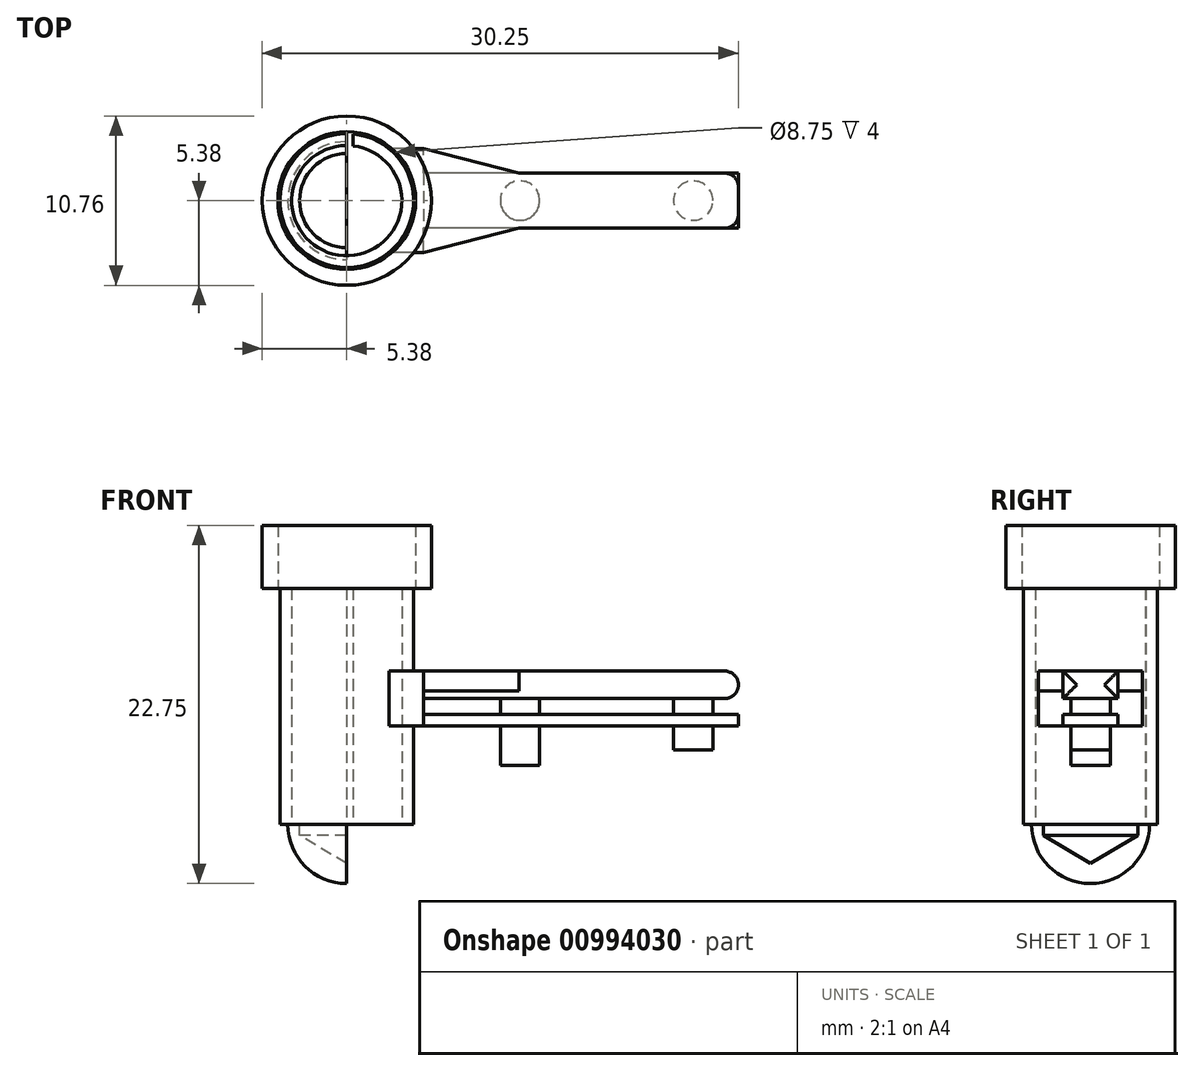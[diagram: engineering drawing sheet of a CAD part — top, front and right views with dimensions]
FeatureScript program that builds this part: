
annotation { "Feature Type Name" : "Feature", "Feature Type Description" : "" }
export const myFeature = defineFeature(function(context is Context, id is Id, definition is map)
    precondition{}
    {
        {
            var Q0;
            Q0=qCreatedBy(makeId("Top.planeOp"),FACE);
            var sketch = newSketch(context, id + "F0", { "sketchPlane" : qUnion([Q0])});
            skCircle(sketch, "E0", {"center": v(0, 0) * mm, "radius": 3.5 * mm});
            skCircle(sketch, "E1", {"center": v(0, 0) * mm, "radius": 4.25 * mm});
            skLineSegment(sketch, "E2", {"start": v(0, -4.25) * mm, "end": v(0, 4.25) * mm});
            skLineSegment(sketch, "E3.bottom", {"start": v(0, 4.35) * mm, "end": v(0.4, 4.35) * mm});
            skLineSegment(sketch, "E3.top", {"start": v(0, 3.35) * mm, "end": v(0.4, 3.35) * mm});
            skLineSegment(sketch, "E3.left", {"start": v(0, 4.35) * mm, "end": v(0, 3.35) * mm});
            skLineSegment(sketch, "E3.right", {"start": v(0.4, 4.35) * mm, "end": v(0.4, 3.35) * mm});
            skSolve(sketch);
        }
        {
            var Q0;
            {var subQ0=sQuery(id+"F0.wireOp",EDGE,"E2");var subQ1=sQuery(id+"F0.wireOp",EDGE,"E0");var subQ2=makeQuery(id+"F0.imprint","INTERSECT",VERTEX,{"disambiguationData":[OD(0.0)],"derivedFrom":[subQ1,subQ0]});Q0=makeQuery(id+"F0.imprint","IMPRINT",FACE,{"disambiguationData":[TD([[makeQuery(id+"F0.imprint","IMPRINT",EDGE,{"disambiguationData":[TD([[subQ2,-1.0]])],"derivedFrom":subQ1}),-1.0]])]});}
            var Q1;
            {var subQ0=sQuery(id+"F0.wireOp",EDGE,"E2");var subQ1=sQuery(id+"F0.wireOp",EDGE,"E0");var subQ2=makeQuery(id+"F0.imprint","INTERSECT",VERTEX,{"disambiguationData":[OD(0.0)],"derivedFrom":[subQ1,subQ0]});Q1=makeQuery(id+"F0.imprint","IMPRINT",FACE,{"disambiguationData":[TD([[makeQuery(id+"F0.imprint","IMPRINT",EDGE,{"disambiguationData":[TD([[subQ2,1.0]])],"derivedFrom":subQ1}),-1.0]])]});}
            extrude(context, id + "F1", {"entities" : qUnion([Q0, Q1]), "endBound" : BoundingType.SYMMETRIC, "depth" : 15 * mm, "offsetDistance" : 25 * mm});
        }
        {
            var Q0;
            Q0=qCreatedBy(makeId("Top.planeOp"),FACE);
            cPlane(context, id + "F2", {"entities" : qUnion([Q0]), "cplaneType" : CPlaneType.OFFSET, "offset" : 7.5 * mm, "oppositeDirection" : true, "width" : 150 * mm, "height" : 150 * mm});
        }
        {
            var Q0;
            Q0=qCreatedBy(id+"F2.planeOp",FACE);
            var sketch = newSketch(context, id + "F3", { "sketchPlane" : qUnion([Q0])});
            skPoint(sketch, "E4.end.orphan", {"position": v(0, -3.75) * mm});
            skPoint(sketch, "E4.start.orphan", {"position": v(0, 3.75) * mm});
            skLineSegment(sketch, "E5.left", {"start": v(0, -3.75) * mm, "end": v(0, -3.75) * mm});
            skLineSegment(sketch, "E6.right", {"start": v(0, 3.75) * mm, "end": v(0, 3.75) * mm});
            skArc(sketch, "E7", {"start": v(0, 3.75) * mm, "mid": v(-3.75, 0) * mm, "end": v(0, -3.75) * mm});
            skLineSegment(sketch, "E8", {"start": v(0, 3.75) * mm, "end": v(0, -3.75) * mm});
            skSolve(sketch);
        }
        {
            var Q0;
            Q0=qCreatedBy(makeId("Top.planeOp"),FACE);
            var sketch = newSketch(context, id + "F4", { "sketchPlane" : qUnion([Q0])});
            skLineSegment(sketch, "E9.bottom", {"start": v(4.87, -3.3) * mm, "end": v(0, -3.3) * mm});
            skLineSegment(sketch, "E9.top", {"start": v(4.87, 3.3) * mm, "end": v(0, 3.3) * mm});
            skLineSegment(sketch, "E9.left", {"start": v(4.87, -3.3) * mm, "end": v(4.87, 3.3) * mm});
            skPoint(sketch, "E9.middle", {"position": v(0, 0) * mm});
            skLineSegment(sketch, "E10", {"start": v(0, 3.3) * mm, "end": v(0, -3.3) * mm});
            skSolve(sketch);
        }
        {
            var Q0;
            Q0=qSketchRegion(id+"F4",true);
            extrude(context, id + "F5", {"entities" : qUnion([Q0]), "operationType" : NewBodyOperationType.ADD, "endBound" : BoundingType.SYMMETRIC, "depth" : 2.5 * mm, "offsetDistance" : 25 * mm});
        }
        {
            var Q0;
            Q0=qCreatedBy(makeId("Top.planeOp"),FACE);
            cPlane(context, id + "F6", {"entities" : qUnion([Q0]), "cplaneType" : CPlaneType.OFFSET, "offset" : 2.18 * mm, "oppositeDirection" : true, "width" : 150 * mm, "height" : 150 * mm});
        }
        {
            var Q0;
            Q0=qCreatedBy(id+"F6.planeOp",FACE);
            var sketch = newSketch(context, id + "F7", { "sketchPlane" : qUnion([Q0])});
            skPoint(sketch, "E11", {"position": v(0, 0) * mm});
            skCircle(sketch, "E12", {"center": v(0, 0) * mm, "radius": 15.5 * mm});
            skSolve(sketch);
        }
        {
            var Q0;
            Q0=makeQuery(id+"F5.opExtrude","SWEPT_FACE",FACE,{"disambiguationData":[OSD([sQuery(id+"F4.wireOp",EDGE,"E9.left")])]});
            cPlane(context, id + "F8", {"entities" : qUnion([Q0]), "cplaneType" : CPlaneType.OFFSET, "offset" : 0 * mm, "width" : 150 * mm, "height" : 150 * mm});
        }
        {
            var Q0;
            Q0=qCreatedBy(id+"F8.planeOp",FACE);
            var sketch = newSketch(context, id + "F9", { "sketchPlane" : qUnion([Q0])});
            skLineSegment(sketch, "E13.bottom", {"start": v(1.75, 0.5) * mm, "end": v(-1.75, 0.5) * mm});
            skLineSegment(sketch, "E13.top", {"start": v(1.75, 1.25) * mm, "end": v(-1.75, 1.25) * mm});
            skLineSegment(sketch, "E13.left", {"start": v(1.75, 0.5) * mm, "end": v(1.75, 1.25) * mm});
            skLineSegment(sketch, "E13.right", {"start": v(-1.75, 0.5) * mm, "end": v(-1.75, 1.25) * mm});
            skPoint(sketch, "E13.middle", {"position": v(0, 0.88) * mm});
            skPoint(sketch, "E14.MirrorP", {"position": v(0, -0.88) * mm});
            skLineSegment(sketch, "E15.bottom", {"start": v(1.75, -1.25) * mm, "end": v(-1.75, -1.25) * mm});
            skLineSegment(sketch, "E15.top", {"start": v(1.75, -0.5) * mm, "end": v(-1.75, -0.5) * mm});
            skLineSegment(sketch, "E15.left", {"start": v(1.75, -1.25) * mm, "end": v(1.75, -0.5) * mm});
            skLineSegment(sketch, "E15.right", {"start": v(-1.75, -1.25) * mm, "end": v(-1.75, -0.5) * mm});
            skLineSegment(sketch, "E16", {"start": v(1.75, -0.5) * mm, "end": v(1.75, 0.5) * mm});
            skSolve(sketch);
        }
        {
            var Q0;
            Q0=makeQuery(id+"F9.imprint","IMPRINT",FACE,{"disambiguationData":[TD([[makeQuery(id+"F9.imprint","IMPRINT",EDGE,{"derivedFrom":sQuery(id+"F9.wireOp",EDGE,"E13.bottom")}),-1.0]])]});
            extrude(context, id + "F10", {"entities" : qUnion([Q0]), "operationType" : NewBodyOperationType.ADD, "depth" : 20 * mm, "offsetDistance" : 25 * mm});
        }
        {
            var Q0;
            {var subQ0=sQuery(id+"F4.wireOp",EDGE,"E9.bottom");var subQ1=sQuery(id+"F4.wireOp",EDGE,"E9.top");var subQ2=sQuery(id+"F4.wireOp",EDGE,"E9.left");Q0=makeQuery(id+"F10.boolean.opBoolean","MERGE",FACE,{"derivedFrom":[makeQuery(id+"F5.boolean.opBoolean","SPLIT",FACE,{"disambiguationData":[TD([makeQuery(id+"F1.opExtrude","SWEPT_FACE",FACE,{"disambiguationData":[OSD([sQuery(id+"F0.wireOp",EDGE,"E1")])]})])],"derivedFrom":makeQuery(id+"F5.opExtrude","CAP_FACE",FACE,{"disambiguationData":[OSD([subQ0,subQ1,subQ2,sQuery(id+"F4.wireOp",EDGE,"E10")])],"isStart":false})}),makeQuery(id+"F10.opExtrude","SWEPT_FACE",FACE,{"disambiguationData":[OSD([sQuery(id+"F9.wireOp",EDGE,"E13.top")])]})]});}
            cPlane(context, id + "F11", {"entities" : qUnion([Q0]), "cplaneType" : CPlaneType.OFFSET, "offset" : 0 * mm, "width" : 150 * mm, "height" : 150 * mm});
        }
        {
            var Q0;
            Q0=qCreatedBy(id+"F11.planeOp",FACE);
            var sketch = newSketch(context, id + "F12", { "sketchPlane" : qUnion([Q0])});
            skPoint(sketch, "E17", {"position": v(11, 0) * mm});
            skPoint(sketch, "E18", {"position": v(22, 0) * mm});
            skLineSegment(sketch, "E19", {"start": v(11, 0) * mm, "end": v(22, 0) * mm});
            skLineSegment(sketch, "E20", {"start": v(0, 0) * mm, "end": v(11, 0) * mm});
            skCircle(sketch, "E21", {"center": v(11, 0) * mm, "radius": 1.25 * mm});
            skCircle(sketch, "E22", {"center": v(22, 0) * mm, "radius": 1.25 * mm});
            skSolve(sketch);
        }
        {
            var Q0;
            {var subQ0=sQuery(id+"F4.wireOp",EDGE,"E9.bottom");var subQ1=sQuery(id+"F4.wireOp",EDGE,"E9.top");var subQ2=sQuery(id+"F4.wireOp",EDGE,"E9.left");Q0=makeQuery(id+"F10.boolean.opBoolean","MERGE",FACE,{"derivedFrom":[makeQuery(id+"F5.boolean.opBoolean","SPLIT",FACE,{"disambiguationData":[TD([makeQuery(id+"F1.opExtrude","SWEPT_FACE",FACE,{"disambiguationData":[OSD([sQuery(id+"F0.wireOp",EDGE,"E1")])]})])],"derivedFrom":makeQuery(id+"F5.opExtrude","CAP_FACE",FACE,{"disambiguationData":[OSD([subQ0,subQ1,subQ2,sQuery(id+"F4.wireOp",EDGE,"E10")])],"isStart":false})}),makeQuery(id+"F10.opExtrude","SWEPT_FACE",FACE,{"disambiguationData":[OSD([sQuery(id+"F9.wireOp",EDGE,"E13.top")])]})]});}
            cPlane(context, id + "F13", {"entities" : qUnion([Q0]), "cplaneType" : CPlaneType.OFFSET, "offset" : 0 * mm, "width" : 150 * mm, "height" : 150 * mm});
        }
        {
            var Q0;
            Q0=makeQuery(id+"F9.imprint","IMPRINT",FACE,{"disambiguationData":[TD([[makeQuery(id+"F9.imprint","IMPRINT",EDGE,{"derivedFrom":sQuery(id+"F9.wireOp",EDGE,"E15.bottom")}),-1.0]])]});
            extrude(context, id + "F14", {"entities" : qUnion([Q0]), "depth" : 20 * mm, "offsetDistance" : 25 * mm});
        }
        {
            var Q0;
            Q0=sQuery(id+"F12.wireOp",VERTEX,"E17");
            var Q1;
            Q1=sQuery(id+"F12.wireOp",VERTEX,"E18");
            var Q2;
            Q2=makeQuery(id+"F14.opExtrude","SWEPT_BODY",BODY,{"disambiguationData":[OSD([sQuery(id+"F9.wireOp",EDGE,"E15.bottom"),sQuery(id+"F9.wireOp",EDGE,"E15.top"),sQuery(id+"F9.wireOp",EDGE,"E15.left"),sQuery(id+"F9.wireOp",EDGE,"E15.right")])]});
            hole(context, id + "F15", {"style" : HoleStyle.SIMPLE, "endStyle" : HoleEndStyle.BLIND, "holeDiameter" : 2.5 * mm, "majorDiameter" : 5 * mm, "holeDepth" : 5 * mm, "isTappedThrough" : true, "tappedDepth" : 12 * mm, "tapClearance" : 3, "startFromSketch" : true, "locations" : qUnion([Q0, Q1]), "scope" : qUnion([Q2])});
        }
        {
            var Q0;
            {var subQ0=sQuery(id+"F12.wireOp",EDGE,"E20");var subQ1=sQuery(id+"F12.wireOp",EDGE,"E19");var subQ2=makeQuery(id+"F12.imprint","INTERSECT",VERTEX,{"derivedFrom":[subQ1,subQ0]});Q0=makeQuery(id+"F12.imprint","IMPRINT",FACE,{"disambiguationData":[TD([[makeQuery(id+"F12.imprint","IMPRINT",EDGE,{"disambiguationData":[TD([[subQ2,-1.0]])],"derivedFrom":subQ1}),-1.0]])]});}
            var Q1;
            {var subQ0=sQuery(id+"F12.wireOp",EDGE,"E20");var subQ1=sQuery(id+"F12.wireOp",EDGE,"E19");var subQ2=makeQuery(id+"F12.imprint","INTERSECT",VERTEX,{"derivedFrom":[subQ1,subQ0]});Q1=makeQuery(id+"F12.imprint","IMPRINT",FACE,{"disambiguationData":[TD([[makeQuery(id+"F12.imprint","IMPRINT",EDGE,{"disambiguationData":[TD([[subQ2,-1.0]])],"derivedFrom":subQ1}),1.0]])]});}
            var Q2;
            Q2=sQuery(id+"F12.wireOp",EDGE,"E21");
            var Q3;
            Q3=sQuery(id+"F12.wireOp",EDGE,"E22");
            extrude(context, id + "F16", {"entities" : qUnion([Q0, Q1]), "operationType" : NewBodyOperationType.ADD, "surfaceOperationType" : NewSurfaceOperationType.ADD, "surfaceEntities" : qUnion([Q2, Q3]), "oppositeDirection" : true, "depth" : 5 * mm, "offsetDistance" : 25 * mm});
        }
        {
            var Q0;
            {var subQ0=makeQuery(id+"F1.opExtrude","SWEPT_FACE",FACE,{"disambiguationData":[OSD([sQuery(id+"F0.wireOp",EDGE,"E1")])]});var subQ1=sQuery(id+"F4.wireOp",EDGE,"E9.bottom");var subQ2=sQuery(id+"F4.wireOp",EDGE,"E9.top");var subQ3=sQuery(id+"F4.wireOp",EDGE,"E9.left");Q0=makeQuery(id+"F45tXFDtNHXHnYf_2.splitOp","SPLIT_SURFACE_INTERSECT",FACE,{"derivedFrom":[subQ0,makeQuery(id+"F26.hole-0.boolean.opBoolean","COPY",FACE,{"derivedFrom":makeQuery(id+"F26.hole-0.opRevolve","SWEPT_FACE",FACE,{"disambiguationData":[OSD([sQuery(id+"F26.hole-0.sketch.wireOp",EDGE,"core_line_2")])]})}),makeQuery(id+"F1.opExtrude","SWEPT_FACE",FACE,{"disambiguationData":[OSD([sQuery(id+"F0.wireOp",EDGE,"E0")])]}),makeQuery(id+"F10.boolean.opBoolean","MERGE",FACE,{"derivedFrom":[makeQuery(id+"F5.boolean.opBoolean","SPLIT",FACE,{"disambiguationData":[TD([subQ0])],"derivedFrom":makeQuery(id+"F5.opExtrude","CAP_FACE",FACE,{"disambiguationData":[OSD([subQ1,subQ2,subQ3,sQuery(id+"F4.wireOp",EDGE,"E10")])],"isStart":false})}),makeQuery(id+"F10.opExtrude","SWEPT_FACE",FACE,{"disambiguationData":[OSD([sQuery(id+"F9.wireOp",EDGE,"E13.top")])]})]})],"isFromBackBody":true});}
            var Q1;
            {var subQ0=sQuery(id+"F4.wireOp",EDGE,"E9.bottom");var subQ1=sQuery(id+"F4.wireOp",EDGE,"E9.top");var subQ2=sQuery(id+"F4.wireOp",EDGE,"E9.left");Q1=makeQuery(id+"F10.boolean.opBoolean","MERGE",FACE,{"derivedFrom":[makeQuery(id+"F5.boolean.opBoolean","SPLIT",FACE,{"disambiguationData":[TD([makeQuery(id+"F1.opExtrude","SWEPT_FACE",FACE,{"disambiguationData":[OSD([sQuery(id+"F0.wireOp",EDGE,"E1")])]})])],"derivedFrom":makeQuery(id+"F5.opExtrude","CAP_FACE",FACE,{"disambiguationData":[OSD([subQ0,subQ1,subQ2,sQuery(id+"F4.wireOp",EDGE,"E10")])],"isStart":false})}),makeQuery(id+"F10.opExtrude","SWEPT_FACE",FACE,{"disambiguationData":[OSD([sQuery(id+"F9.wireOp",EDGE,"E13.top")])]})]});}
            extrude(context, id + "F17", {"entities" : qUnion([Q0, Q1]), "operationType" : NewBodyOperationType.ADD, "depth" : 1 * mm, "offsetDistance" : 25 * mm});
        }
        {
            var Q0;
            Q0=makeQuery(id+"F12.imprint","IMPRINT",FACE,{"disambiguationData":[TD([[makeQuery(id+"F12.imprint","IMPRINT",EDGE,{"derivedFrom":sQuery(id+"F12.wireOp",EDGE,"E22")}),1.0]])]});
            extrude(context, id + "F18", {"entities" : qUnion([Q0]), "operationType" : NewBodyOperationType.ADD, "oppositeDirection" : true, "depth" : 4 * mm, "offsetDistance" : 25 * mm});
        }
        {
            var Q0;
            Q0=makeQuery(id+"F17.opExtrude","CAP_FACE",FACE,{"disambiguationData":[OSD([sQuery(id+"F0.wireOp",EDGE,"E0"),sQuery(id+"F0.wireOp",EDGE,"E1"),sQuery(id+"F4.wireOp",EDGE,"E9.bottom"),sQuery(id+"F4.wireOp",EDGE,"E9.top"),sQuery(id+"F4.wireOp",EDGE,"E9.left"),sQuery(id+"F4.wireOp",EDGE,"E10"),sQuery(id+"F26.hole-0.sketch.wireOp",EDGE,"core_line_2"),sQuery(id+"F9.wireOp",EDGE,"E13.top")])],"isStart":false});
            var sketch = newSketch(context, id + "F19", { "sketchPlane" : qUnion([Q0])});
            skLineSegment(sketch, "E23", {"start": v(4.87, 3.3) * mm, "end": v(4.87, 1.75) * mm});
            skLineSegment(sketch, "E24", {"start": v(4.87, 1.75) * mm, "end": v(10.95, 1.75) * mm});
            skLineSegment(sketch, "E25", {"start": v(10.95, 1.75) * mm, "end": v(4.87, 3.3) * mm});
            skLineSegment(sketch, "E26", {"start": v(4.87, -3.3) * mm, "end": v(4.87, -1.75) * mm});
            skLineSegment(sketch, "E27", {"start": v(4.87, -1.75) * mm, "end": v(10.95, -1.75) * mm});
            skLineSegment(sketch, "E28", {"start": v(10.95, -1.75) * mm, "end": v(4.87, -3.3) * mm});
            skSolve(sketch);
        }
        {
            var Q0;
            Q0=makeQuery(id+"F19.imprint","IMPRINT",FACE,{"disambiguationData":[TD([[makeQuery(id+"F19.imprint","IMPRINT",EDGE,{"derivedFrom":sQuery(id+"F19.wireOp",EDGE,"E23")}),-1.0]])]});
            var Q1;
            Q1=makeQuery(id+"F19.imprint","IMPRINT",FACE,{"disambiguationData":[TD([[makeQuery(id+"F19.imprint","IMPRINT",EDGE,{"derivedFrom":sQuery(id+"F19.wireOp",EDGE,"E26")}),-1.0]])]});
            extrude(context, id + "F20", {"entities" : qUnion([Q0, Q1]), "operationType" : NewBodyOperationType.ADD, "oppositeDirection" : true, "depth" : 1.25 * mm, "offsetDistance" : 25 * mm});
        }
        {
            var Q0;
            {var subQ0=sQuery(id+"F4.wireOp",EDGE,"E10");var subQ1=sQuery(id+"F4.wireOp",EDGE,"E9.top");Q0=makeQuery(id+"F5.boolean.opBoolean","SPLIT",FACE,{"disambiguationData":[TD([makeQuery(id+"F1.opExtrude","SWEPT_FACE",FACE,{"disambiguationData":[OSD([sQuery(id+"F0.wireOp",EDGE,"E0")])]})])],"derivedFrom":makeQuery(id+"F5.opExtrude","CAP_FACE",FACE,{"disambiguationData":[OSD([sQuery(id+"F4.wireOp",EDGE,"E9.bottom"),subQ1,sQuery(id+"F4.wireOp",EDGE,"E9.left"),subQ0])],"isStart":false})});}
            extrude(context, id + "F21", {"entities" : qUnion([Q0]), "operationType" : NewBodyOperationType.REMOVE, "oppositeDirection" : true, "depth" : 25 * mm, "offsetDistance" : 25 * mm});
        }
        {
            var Q0;
            Q0=makeQuery(id+"F1.opExtrude","CAP_FACE",FACE,{"disambiguationData":[OSD([sQuery(id+"F0.wireOp",EDGE,"E0"),sQuery(id+"F0.wireOp",EDGE,"E1"),sQuery(id+"F0.wireOp",EDGE,"E3.left"),sQuery(id+"F0.wireOp",EDGE,"E3.right")])],"isStart":false});
            var sketch = newSketch(context, id + "F22", { "sketchPlane" : qUnion([Q0])});
            skCircle(sketch, "E29", {"center": v(0, 0) * mm, "radius": 4.38 * mm});
            skCircle(sketch, "E30", {"center": v(0, 0) * mm, "radius": 5.38 * mm});
            skSolve(sketch);
        }
        {
            var Q0;
            Q0=makeQuery(id+"F22.imprint","IMPRINT",FACE,{"disambiguationData":[TD([[makeQuery(id+"F22.imprint","IMPRINT",EDGE,{"derivedFrom":sQuery(id+"F22.wireOp",EDGE,"E29")}),-1.0]])]});
            extrude(context, id + "F23", {"entities" : qUnion([Q0]), "depth" : 4 * mm, "offsetDistance" : 25 * mm});
        }
        {
            var Q0;
            {var subQ0=sQuery(id+"F9.wireOp",EDGE,"E13.top");Q0=makeQuery(id+"F17.boolean.opBoolean","MERGE",FACE,{"derivedFrom":[makeQuery(id+"F10.opExtrude","CAP_FACE",FACE,{"disambiguationData":[OSD([sQuery(id+"F9.wireOp",EDGE,"E13.bottom"),subQ0,sQuery(id+"F9.wireOp",EDGE,"E13.left"),sQuery(id+"F9.wireOp",EDGE,"E13.right")])],"isStart":false}),makeQuery(id+"F17.opExtrude","SWEPT_FACE",FACE,{"disambiguationData":[OSD([subQ0])]})]});}
            fillet(context, id + "F24", {"entities" : qUnion([Q0]), "radius" : 0.88 * mm, "tangentPropagation" : true, "allowEdgeOverflow" : false});
        }
        {
            var Q0;
            Q0=makeQuery(id+"F3.imprint","IMPRINT",FACE,{"disambiguationData":[TD([[makeQuery(id+"F3.imprint","IMPRINT",EDGE,{"derivedFrom":sQuery(id+"F3.wireOp",EDGE,"E7")}),1.0]])]});
            var Q1;
            Q1=sQuery(id+"F3.wireOp",EDGE,"E8");
            revolve(context, id + "F25", {"operationType" : NewBodyOperationType.ADD, "surfaceOperationType" : NewSurfaceOperationType.NEW, "entities" : qUnion([Q0]), "axis" : qUnion([Q1]), "revolveType" : RevolveType.ONE_DIRECTION, "angle" : 90 * degree});
        }
        {
            var Q0;
            Q0=sQuery(id+"F7.wireOp",VERTEX,"E11");
            var Q1;
            Q1=makeQuery(id+"F1.opExtrude","SWEPT_BODY",BODY,{"disambiguationData":[OSD([sQuery(id+"F0.wireOp",EDGE,"E0"),sQuery(id+"F0.wireOp",EDGE,"E1"),sQuery(id+"F0.wireOp",EDGE,"E3.left"),sQuery(id+"F0.wireOp",EDGE,"E3.right")])]});
            hole(context, id + "F26", {"style" : HoleStyle.SIMPLE, "endStyle" : HoleEndStyle.BLIND, "holeDiameter" : 6 * mm, "majorDiameter" : 5 * mm, "holeDepth" : 6 * mm, "isTappedThrough" : true, "tappedDepth" : 12 * mm, "tapClearance" : 3, "startFromSketch" : true, "locations" : qUnion([Q0]), "scope" : qUnion([Q1])});
        }
    });
